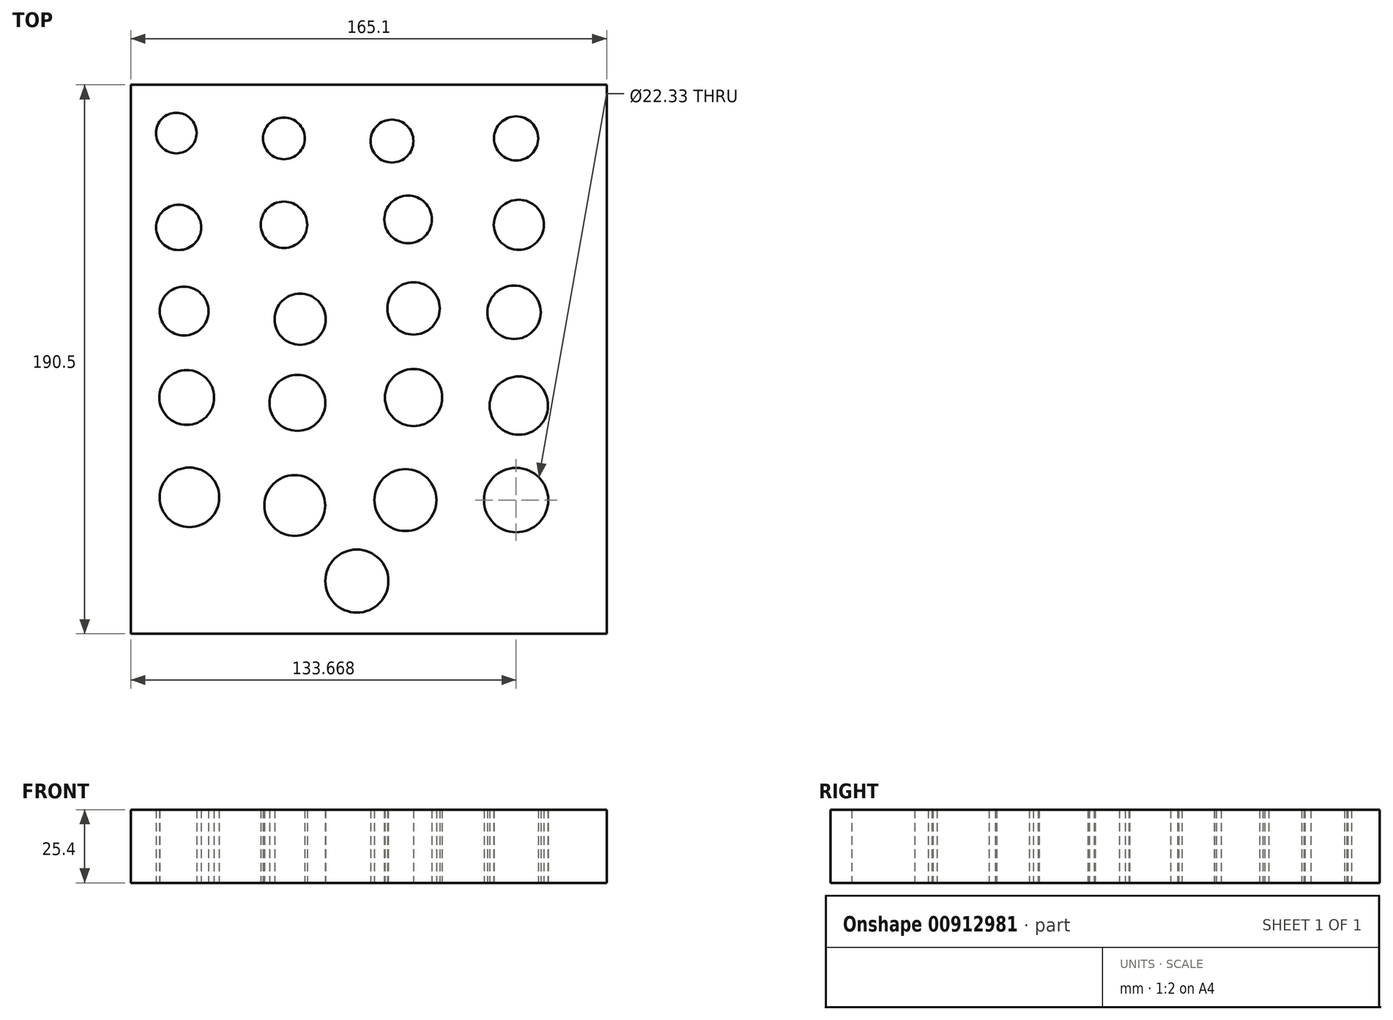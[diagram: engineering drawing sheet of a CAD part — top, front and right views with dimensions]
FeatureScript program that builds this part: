
annotation { "Feature Type Name" : "Feature", "Feature Type Description" : "" }
export const myFeature = defineFeature(function(context is Context, id is Id, definition is map)
    precondition{}
    {
        {
            var Q0;
            Q0=qCreatedBy(makeId("Top.planeOp"),FACE);
            var sketch = newSketch(context, id + "F0", { "sketchPlane" : qUnion([Q0])});
            skCircle(sketch, "E0", {"center": v(-555.92, -87.42) * mm, "radius": 7.04 * mm});
            skCircle(sketch, "E1", {"center": v(-518.58, -89.27) * mm, "radius": 7.24 * mm});
            skCircle(sketch, "E2", {"center": v(-481.12, -90.2) * mm, "radius": 7.44 * mm});
            skCircle(sketch, "E3", {"center": v(-555.1, -120.17) * mm, "radius": 7.85 * mm});
            skCircle(sketch, "E4", {"center": v(-518.58, -119.24) * mm, "radius": 8.05 * mm});
            skLineSegment(sketch, "E5.bottom", {"start": v(-571.7, -70.68) * mm, "end": v(-406.6, -70.68) * mm});
            skLineSegment(sketch, "E5.top", {"start": v(-571.7, -261.18) * mm, "end": v(-406.6, -261.18) * mm});
            skLineSegment(sketch, "E5.left", {"start": v(-571.7, -70.68) * mm, "end": v(-571.7, -261.18) * mm});
            skLineSegment(sketch, "E5.right", {"start": v(-406.6, -70.68) * mm, "end": v(-406.6, -261.18) * mm});
            skCircle(sketch, "E6", {"center": v(-438.03, -89.27) * mm, "radius": 7.65 * mm});
            skCircle(sketch, "E7", {"center": v(-475.5, -117.36) * mm, "radius": 8.25 * mm});
            skCircle(sketch, "E8", {"center": v(-553.23, -149.2) * mm, "radius": 8.46 * mm});
            skCircle(sketch, "E9", {"center": v(-437.1, -119.24) * mm, "radius": 8.67 * mm});
            skCircle(sketch, "E10", {"center": v(-512.96, -152.02) * mm, "radius": 8.88 * mm});
            skCircle(sketch, "E11", {"center": v(-473.62, -148.27) * mm, "radius": 9.1 * mm});
            skCircle(sketch, "E12", {"center": v(-438.73, -149.63) * mm, "radius": 9.26 * mm});
            skCircle(sketch, "E13", {"center": v(-552.3, -179.18) * mm, "radius": 9.5 * mm});
            skCircle(sketch, "E14", {"center": v(-513.9, -181.05) * mm, "radius": 9.7 * mm});
            skCircle(sketch, "E15", {"center": v(-473.62, -179.18) * mm, "radius": 9.92 * mm});
            skCircle(sketch, "E16", {"center": v(-437.1, -182) * mm, "radius": 10.12 * mm});
            skCircle(sketch, "E17", {"center": v(-551.36, -213.84) * mm, "radius": 10.34 * mm});
            skCircle(sketch, "E18", {"center": v(-514.83, -216.64) * mm, "radius": 10.54 * mm});
            skLineSegment(sketch, "E19", {"start": v(-571.7, -172.28) * mm, "end": v(-406.6, -172.28) * mm});
            skCircle(sketch, "E20", {"center": v(-476.43, -214.77) * mm, "radius": 10.74 * mm});
            skCircle(sketch, "E21", {"center": v(-493.3, -242.87) * mm, "radius": 10.95 * mm});
            skCircle(sketch, "E22", {"center": v(-438.03, -214.77) * mm, "radius": 11.16 * mm});
            skSolve(sketch);
        }
        {
            var Q0;
            Q0=makeQuery(id+"F0.imprint","IMPRINT",FACE,{"disambiguationData":[TD([[makeQuery(id+"F0.imprint","IMPRINT",EDGE,{"derivedFrom":sQuery(id+"F0.wireOp",EDGE,"E0")}),-1.0]])]});
            var Q1;
            {var subQ11=sQuery(id+"F0.wireOp",EDGE,"E5.top");Q1=makeQuery(id+"F0.imprint","IMPRINT",FACE,{"disambiguationData":[TD([[makeQuery(id+"F0.imprint","IMPRINT",EDGE,{"derivedFrom":subQ11}),1.0]])]});}
            extrude(context, id + "F1", {"entities" : qUnion([Q0, Q1]), "depth" : 25.4 * mm, "offsetDistance" : 25.4 * mm});
        }
    });
